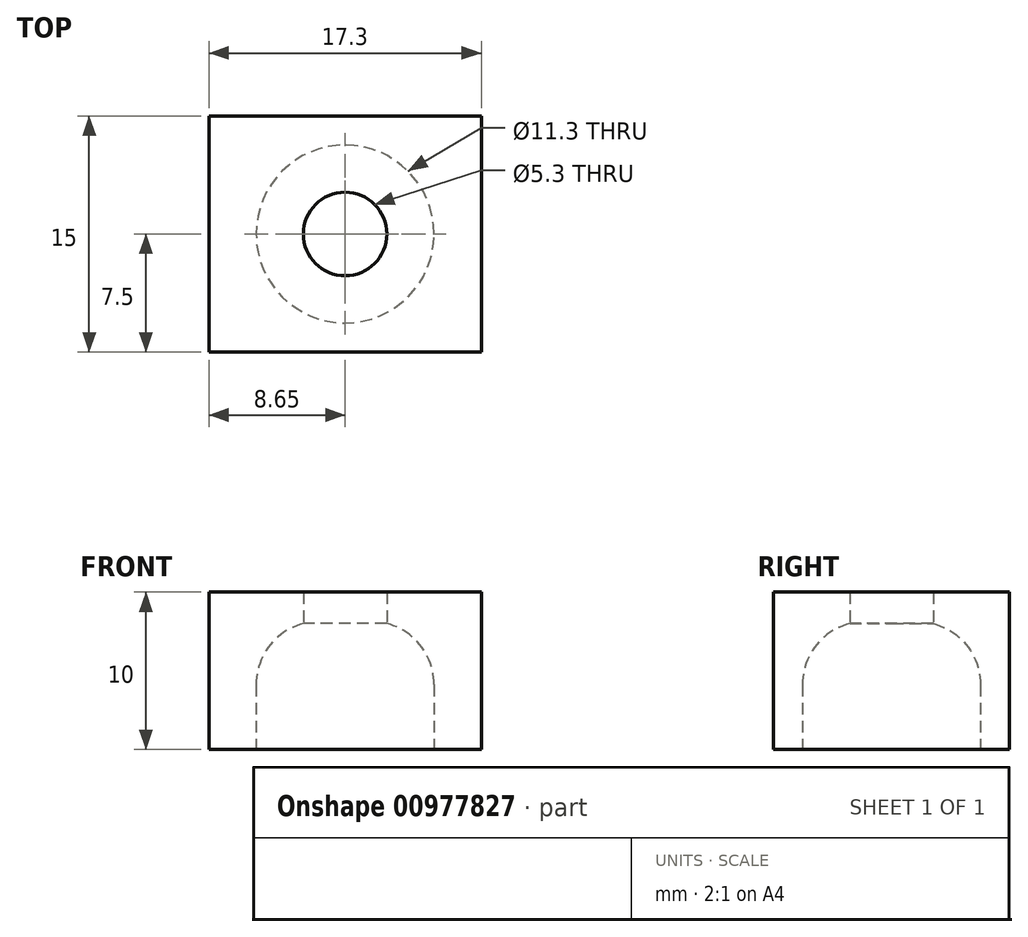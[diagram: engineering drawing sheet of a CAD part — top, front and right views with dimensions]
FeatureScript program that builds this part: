
annotation { "Feature Type Name" : "Feature", "Feature Type Description" : "" }
export const myFeature = defineFeature(function(context is Context, id is Id, definition is map)
    precondition{}
    {
        {
            var Q0;
            Q0=qCreatedBy(makeId("Top.planeOp"),FACE);
            var sketch = newSketch(context, id + "F0", { "sketchPlane" : qUnion([Q0])});
            skCircle(sketch, "E0", {"center": v(0, 0) * mm, "radius": 5.65 * mm});
            skLineSegment(sketch, "E1.bottom", {"start": v(8.65, 7.5) * mm, "end": v(-8.65, 7.5) * mm});
            skLineSegment(sketch, "E1.top", {"start": v(8.65, -7.5) * mm, "end": v(-8.65, -7.5) * mm});
            skLineSegment(sketch, "E1.left", {"start": v(8.65, 7.5) * mm, "end": v(8.65, -7.5) * mm});
            skLineSegment(sketch, "E1.right", {"start": v(-8.65, 7.5) * mm, "end": v(-8.65, -7.5) * mm});
            skPoint(sketch, "E2.end.orphan", {"position": v(8.65, 0.61) * mm});
            skPoint(sketch, "E2.start.orphan", {"position": v(5.65, 0) * mm});
            skSolve(sketch);
        }
        {
            var Q0;
            Q0=makeQuery(id+"F0.imprint","IMPRINT",FACE,{"disambiguationData":[TD([[makeQuery(id+"F0.imprint","IMPRINT",EDGE,{"derivedFrom":sQuery(id+"F0.wireOp",EDGE,"E0")}),-1.0]])]});
            var Q1;
            Q1=makeQuery(id+"F0.imprint","IMPRINT",FACE,{"disambiguationData":[TD([[makeQuery(id+"F0.imprint","IMPRINT",EDGE,{"derivedFrom":sQuery(id+"F0.wireOp",EDGE,"E0")}),1.0]])]});
            extrude(context, id + "F1", {"entities" : qUnion([Q0, Q1]), "depth" : 10 * mm, "offsetDistance" : 25 * mm});
        }
        {
            var Q0;
            Q0=makeQuery(id+"F0.imprint","IMPRINT",FACE,{"disambiguationData":[TD([[makeQuery(id+"F0.imprint","IMPRINT",EDGE,{"derivedFrom":sQuery(id+"F0.wireOp",EDGE,"E0")}),1.0]])]});
            extrude(context, id + "F2", {"entities" : qUnion([Q0]), "operationType" : NewBodyOperationType.REMOVE, "depth" : 8 * mm, "offsetDistance" : 25 * mm});
        }
        {
            var Q0;
            Q0=makeQuery(id+"F0.imprint","IMPRINT",FACE,{"disambiguationData":[TD([[makeQuery(id+"F0.imprint","IMPRINT",EDGE,{"derivedFrom":sQuery(id+"F0.wireOp",EDGE,"E0")}),1.0]])]});
            var sketch = newSketch(context, id + "F3", { "sketchPlane" : qUnion([Q0])});
            skCircle(sketch, "E3", {"center": v(0, 0) * mm, "radius": 2.65 * mm});
            skSolve(sketch);
        }
        {
            var Q0;
            Q0=makeQuery(id+"F3.imprint","IMPRINT",FACE,{"disambiguationData":[TD([[makeQuery(id+"F3.imprint","IMPRINT",EDGE,{"derivedFrom":sQuery(id+"F3.wireOp",EDGE,"E3")}),1.0]])]});
            extrude(context, id + "F4", {"entities" : qUnion([Q0]), "operationType" : NewBodyOperationType.REMOVE, "depth" : 16.1 * mm, "offsetDistance" : 25 * mm});
        }
        {
            var Q0;
            Q0=makeQuery(id+"F2.boolean.opBoolean","COPY",EDGE,{"derivedFrom":makeQuery(id+"F2.opExtrude","CAP_EDGE",EDGE,{"disambiguationData":[OSD([sQuery(id+"F0.wireOp",EDGE,"E0")])],"isStart":false})});
            fillet(context, id + "F5", {"entities" : qUnion([Q0]), "radius" : 4 * mm, "tangentPropagation" : true, "allowEdgeOverflow" : false});
        }
    });
